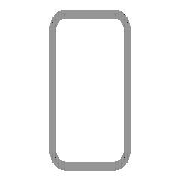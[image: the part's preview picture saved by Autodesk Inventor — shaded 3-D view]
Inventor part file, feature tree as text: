
AUTODESK INVENTOR PART (.ipt)
format: ipt  version: 2025 (Build 290162010, 162A)  size: 157,184 bytes
history: native  units: mm (DEFAULTED — no unit token found)
features: other x3, projected_geometry x3, sketch x2, extrude x1, plane x1
ambient origin geometry x8: Origin, YZ Plane, XZ Plane, XY Plane, X Axis, Y Axis, Z Axis, Center Point
bodies: Solid1 (feature_tree), Body (feature_tree)
feature tree (10):
  other  "Driven Length"
  other  "Start plane"
  other  "End plane"
  extrude  "Extrusion2"  TaperAngle=0.0deg  [1 undecoded]
  sketch  "Sketch3"  dims[d3=1000.0mm d4=0.0mm]
  plane  "Work Plane3"
  sketch  "Sketch5"  dims[d7=6.0mm d9=40.0mm d11=60.0mm d12=3.0mm d13=-0.0mm d14=1000.0mm d15=20.0mm d16=30.0mm d17=90.0deg d18=1000.0mm d19=45.0deg d20=45.0deg d21=0.0mm d22=0.0mm]
  projected_geometry  "Projected Loop1"
  projected_geometry  "Projected Loop2"
  projected_geometry  "Projected Loop3"
note: 1 required parameter value undecoded (feature->parameter linkage not recoverable at this tier; creation-order binding heuristic only, values carry confidence <= 0.55)
